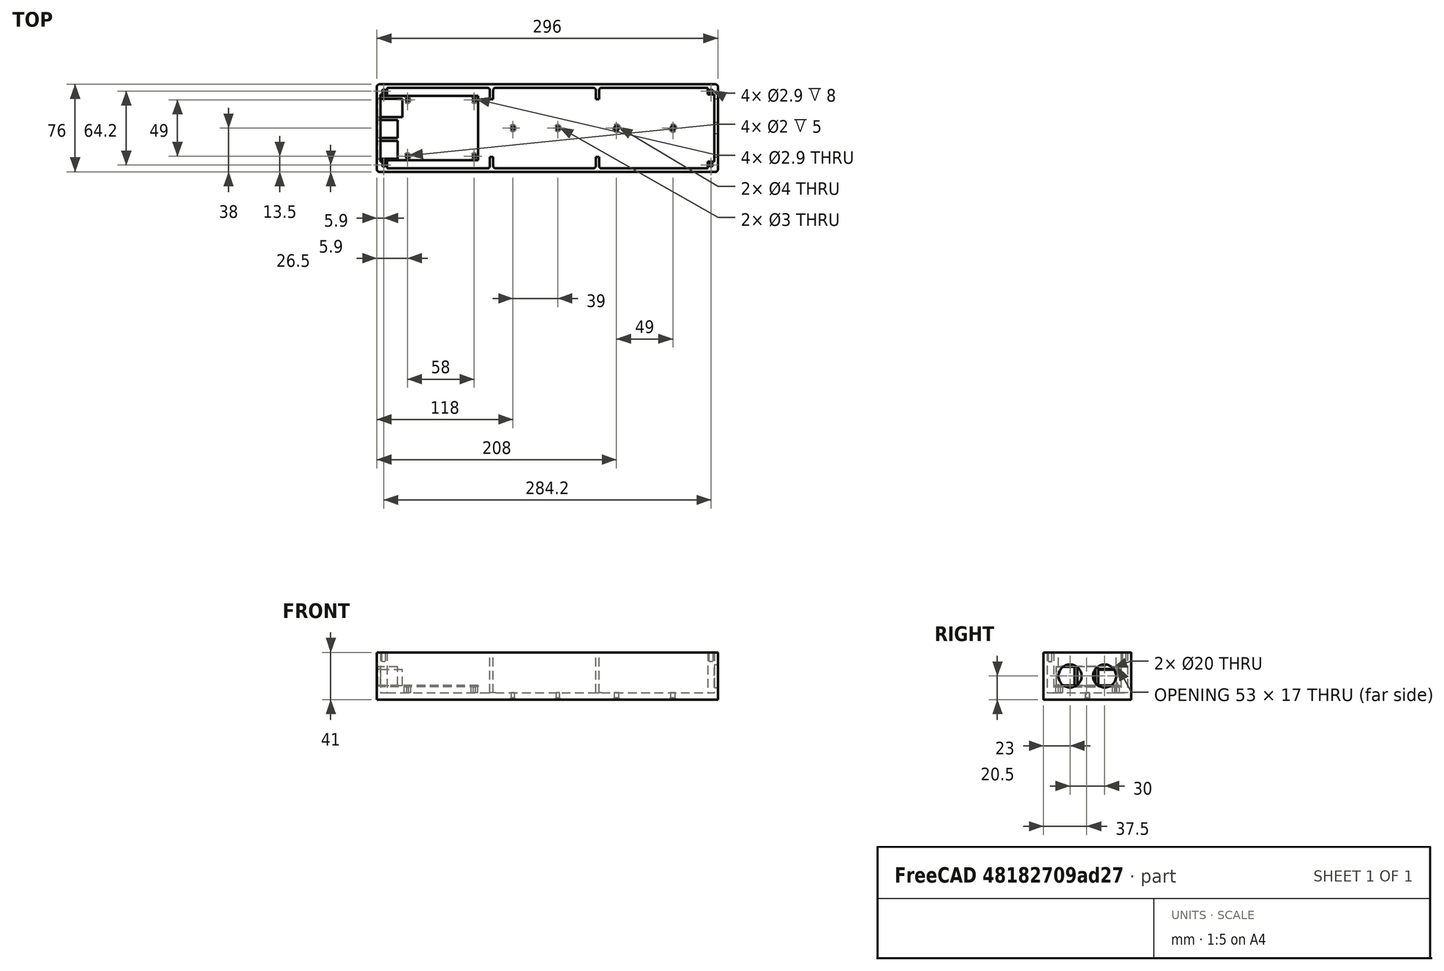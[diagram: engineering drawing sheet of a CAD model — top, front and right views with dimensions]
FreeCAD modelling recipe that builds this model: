
FCSTD DOCUMENT  (FreeCAD 0.19R24276 (Git))
Label: Octopi Enclosure
License: All rights reserved
LicenseURL: http://en.wikipedia.org/wiki/All_rights_reserved
objects: Sketcher::SketchObject×12, PartDesign::Pad×6, PartDesign::Pocket×5, PartDesign::Body×2, PartDesign::Fillet×2, TechDraw::DrawViewDimension×2, Spreadsheet::Sheet×1, PartDesign::Chamfer×1, TechDraw::DrawSVGTemplate×1, TechDraw::DrawViewPart×1, TechDraw::DrawPage×1
note: 42 computed .brp shape members not serialized (recipe doc carries the construction recipe); baked Part::Feature solids carry a one-line shape summary decoded from their .brp

FEATURE [Spreadsheet::Sheet] Spreadsheet
  cells = A2=Internal length; B2(Length)=290; C2=Length; A3=Internal width; B3(Width)=70; C3=Width; A4=Internal height; B4(Height)=35; C4=Height; A5=Wall thickness; B5(Wall)=3; C5=Wall; A6=Lid screw dia; B6(LidScrewDia)=2.9; C6=LidScrewDia; A7=Corner radius; B7(CornerRadius)=2; C7=CornerRadius
FEATURE [Sketcher::SketchObject] Sketch  label="External"
  FullyConstrained = true
  MapMode = 5
  Support = -> [XY_Plane]
  expr: Constraints[8] = <<Spreadsheet>>.Wall
  expr: Constraints[9] = <<Spreadsheet>>.Wall
  expr: Constraints[10] = <<Spreadsheet>>.Width + <<Spreadsheet>>.Wall * 2
  expr: Constraints[11] = <<Spreadsheet>>.Length + <<Spreadsheet>>.Wall * 2
  sketch-geometry (4):
    g0: LineSegment StartX=-3 StartY=73 StartZ=0 EndX=293 EndY=73 EndZ=0
    g1: LineSegment StartX=293 StartY=73 StartZ=0 EndX=293 EndY=-3 EndZ=0
    g2: LineSegment StartX=293 StartY=-3 StartZ=0 EndX=-3 EndY=-3 EndZ=0
    g3: LineSegment StartX=-3 StartY=-3 StartZ=0 EndX=-3 EndY=73 EndZ=0
  constraints (12):
    c: Coincident(g0,g1)
    c: Coincident(g1,g2)
    c: Coincident(g2,g3)
    c: Coincident(g3,g0)
    c: Horizontal(g0)
    c: Horizontal(g2)
    c: Vertical(g1)
    c: Vertical(g3)
    c: DistanceY(g2,g-1) = 3
    c: DistanceX(g2,g-1) = 3
    c: DistanceY(g3,g3) = 76
    c: DistanceX(g0,g0) = 296
FEATURE [PartDesign::Pad] Pad  label="Body001"
  Direction = (1,1,1)
  Length = 41
  Length2 = 100
  Profile = -> Sketch
  Type = 0
  expr: Length = <<Spreadsheet>>.Height + <<Spreadsheet>>.Wall * 2
FEATURE [Sketcher::SketchObject] Sketch001  label="Internal"
  FullyConstrained = true
  MapMode = 5
  Placement = pos=(0,0,41) rot=(0,0,1;0rad)
  Support = -> [Pad]
  expr: Constraints[26] = <<Spreadsheet>>.Width
  expr: Constraints[27] = <<Spreadsheet>>.Length
  expr: Constraints[28] = <<Spreadsheet>>.LidScrewDia * 2
  sketch-geometry (12):
    g0: LineSegment StartX=5.8 StartY=70 StartZ=0 EndX=284.2 EndY=70 EndZ=0
    g1: LineSegment StartX=284.2 StartY=70 StartZ=0 EndX=284.2 EndY=64.2 EndZ=0
    g2: LineSegment StartX=284.2 StartY=64.2 StartZ=0 EndX=290 EndY=64.2 EndZ=0
    g3: LineSegment StartX=290 StartY=64.2 StartZ=0 EndX=290 EndY=5.8 EndZ=0
    g4: LineSegment StartX=290 StartY=5.8 StartZ=0 EndX=284.2 EndY=5.8 EndZ=0
    g5: LineSegment StartX=284.2 StartY=5.8 StartZ=0 EndX=284.2 EndY=0 EndZ=0
    g6: LineSegment StartX=284.2 StartY=0 StartZ=0 EndX=5.8 EndY=0 EndZ=0
    g7: LineSegment StartX=5.8 StartY=0 StartZ=0 EndX=5.8 EndY=5.8 EndZ=0
    g8: LineSegment StartX=5.8 StartY=5.8 StartZ=0 EndX=0 EndY=5.8 EndZ=0
    g9: LineSegment StartX=0 StartY=5.8 StartZ=0 EndX=0 EndY=64.2 EndZ=0
    g10: LineSegment StartX=0 StartY=64.2 StartZ=0 EndX=5.8 EndY=64.2 EndZ=0
    g11: LineSegment StartX=5.8 StartY=70 StartZ=0 EndX=5.8 EndY=64.2 EndZ=0
  constraints (36):
    c: Horizontal(g0)
    c: Coincident(g0,g1)
    c: Vertical(g1)
    c: Coincident(g1,g2)
    c: Horizontal(g2)
    c: Coincident(g2,g3)
    c: Vertical(g3)
    c: Coincident(g3,g4)
    c: Horizontal(g4)
    c: Coincident(g4,g5)
    c: Vertical(g5)
    c: Coincident(g5,g6)
    c: Horizontal(g6)
    c: Coincident(g6,g7)
    c: Vertical(g7)
    c: Coincident(g7,g8)
    c: Horizontal(g8)
    c: Coincident(g8,g9)
    c: Vertical(g9)
    c: Coincident(g9,g10)
    c: Horizontal(g10)
    c: Coincident(g11,g0)
    c: Coincident(g11,g10)
    c: Vertical(g11)
    c: PointOnObject(g8,g-2)
    c: PointOnObject(g6,g-1)
    c: DistanceY(g6,g0) = 70
    c: DistanceX(g8,g3) = 290
    c: DistanceY(g7,g7) = 5.8
    c: Equal(g7,g8)
    c: Equal(g10,g7)
    c: Equal(g11,g7)
    c: Equal(g7,g5)
    c: Equal(g5,g4)
    c: Equal(g5,g2)
    c: Equal(g5,g1)
FEATURE [PartDesign::Pocket] Pocket  label="Inside space"
  BaseFeature = -> Pad
  Length = 35
  Length2 = 100
  Profile = -> Sketch001
  Type = 0
  expr: Length = <<Spreadsheet>>.Height
FEATURE [Sketcher::SketchObject] Sketch002  label="Raspberry PI"
  AttachmentOffset = pos=(85,63,0) rot=(0,0,1;3.14159rad)
  FullyConstrained = true
  MapMode = 5
  Placement = pos=(85,63,6) rot=(0,0,1;3.14159rad)
  Support = -> [Pocket]
  expr: Constraints[10] = <<Spreadsheet>>.LidScrewDia
  expr: Constraints[18] = 6
  expr: .AttachmentOffset.Base.y = 56 + (<<Spreadsheet>>.Width - 56) / 2
  sketch-geometry (12):
    g0: LineSegment StartX=0 StartY=0 StartZ=0 EndX=85 EndY=0 EndZ=0
    g1: LineSegment StartX=85 StartY=0 StartZ=0 EndX=85 EndY=56 EndZ=0
    g2: LineSegment StartX=85 StartY=56 StartZ=0 EndX=0 EndY=56 EndZ=0
    g3: LineSegment StartX=0 StartY=56 StartZ=0 EndX=0 EndY=0 EndZ=0
    g4: Circle CenterX=3.5 CenterY=3.5 CenterZ=0 NormalX=0 NormalY=0 NormalZ=1 AngleXU=0 Radius=1.45
    g5: Circle CenterX=3.5 CenterY=52.5 CenterZ=0 NormalX=0 NormalY=0 NormalZ=1 AngleXU=0 Radius=1.45
    g6: Circle CenterX=61.5 CenterY=52.5 CenterZ=0 NormalX=0 NormalY=0 NormalZ=1 AngleXU=0 Radius=1.45
    g7: Circle CenterX=61.5 CenterY=3.5 CenterZ=0 NormalX=0 NormalY=0 NormalZ=1 AngleXU=0 Radius=1.45
    g8: Circle CenterX=3.5 CenterY=3.5 CenterZ=0 NormalX=0 NormalY=0 NormalZ=1 AngleXU=0 Radius=3
    g9: Circle CenterX=3.5 CenterY=52.5 CenterZ=0 NormalX=0 NormalY=0 NormalZ=1 AngleXU=0 Radius=3
    g10: Circle CenterX=61.5 CenterY=3.5 CenterZ=0 NormalX=0 NormalY=0 NormalZ=1 AngleXU=0 Radius=3
    g11: Circle CenterX=61.5 CenterY=52.5 CenterZ=0 NormalX=0 NormalY=0 NormalZ=1 AngleXU=0 Radius=3
  constraints (31):
    c: Coincident(g0,g1)
    c: Coincident(g1,g2)
    c: Coincident(g2,g3)
    c: Coincident(g3,g0)
    c: Horizontal(g0)
    c: Horizontal(g2)
    c: Vertical(g1)
    c: Vertical(g3)
    c: DistanceX(g2,g2) = 85
    c: DistanceY(g1,g1) = 56
    c: Diameter(g4) = 2.9
    c: DistanceX(g0,g4) = 3.5
    c: DistanceY(g0,g4) = 3.5
    c: Equal(g4,g5)
    c: Equal(g5,g6)
    c: Equal(g6,g7)
    c: DistanceY(g5,g2) = 3.5
    c: Coincident(g8,g4)
    c: Diameter(g8) = 6
    c: Equal(g9,g11)
    c: Equal(g11,g10)
    c: Equal(g10,g8)
    c: Coincident(g9,g5)
    c: Coincident(g11,g6)
    c: Coincident(g10,g7)
    c: Coincident(g0,g-1)
    c: DistanceX(g4,g7) = 58
    c: Vertical(g7,g6)
    c: Horizontal(g5,g6)
    c: Horizontal(g4,g7)
    c: Vertical(g5,g4)
FEATURE [Sketcher::SketchObject] Sketch003  label="Raspberry PI001"
  AttachmentOffset = pos=(85,63,0) rot=(0,0,1;3.14159rad)
  FullyConstrained = true
  expr: .AttachmentOffset.Base.y = 56 + (<<Spreadsheet>>.Width - 56) / 2
  expr: Constraints[10] = <<Spreadsheet>>.LidScrewDia
  sketch-geometry (8):
    g0: LineSegment StartX=0 StartY=0 StartZ=0 EndX=85 EndY=0 EndZ=0
    g1: LineSegment StartX=85 StartY=0 StartZ=0 EndX=85 EndY=56 EndZ=0
    g2: LineSegment StartX=85 StartY=56 StartZ=0 EndX=0 EndY=56 EndZ=0
    g3: LineSegment StartX=0 StartY=56 StartZ=0 EndX=0 EndY=0 EndZ=0
    g4: Circle CenterX=3.5 CenterY=3.5 CenterZ=0 NormalX=0 NormalY=0 NormalZ=1 AngleXU=0 Radius=1.45
    g5: Circle CenterX=3.5 CenterY=52.5 CenterZ=0 NormalX=0 NormalY=0 NormalZ=1 AngleXU=0 Radius=1.45
    g6: Circle CenterX=61.5 CenterY=52.5 CenterZ=0 NormalX=0 NormalY=0 NormalZ=1 AngleXU=0 Radius=1.45
    g7: Circle CenterX=61.5 CenterY=3.5 CenterZ=0 NormalX=0 NormalY=0 NormalZ=1 AngleXU=0 Radius=1.45
  constraints (23):
    c: Coincident(g0,g1)
    c: Coincident(g1,g2)
    c: Coincident(g2,g3)
    c: Coincident(g3,g0)
    c: Horizontal(g0)
    c: Horizontal(g2)
    c: Vertical(g1)
    c: Vertical(g3)
    c: DistanceX(g2,g2) = 85
    c: DistanceY(g1,g1) = 56
    c: Diameter(g4) = 2.9
    c: DistanceX(g0,g4) = 3.5
    c: DistanceY(g0,g4) = 3.5
    c: Equal(g4,g5)
    c: Equal(g5,g6)
    c: Equal(g6,g7)
    c: DistanceY(g5,g2) = 3.5
    c: Coincident(g0,g-1)
    c: DistanceX(g4,g7) = 58
    c: Vertical(g7,g6)
    c: Horizontal(g5,g6)
    c: Horizontal(g4,g7)
    c: Vertical(g5,g4)
FEATURE [PartDesign::Pad] Pad001  label="PCB"
  Direction = (1,1,1)
  Length = 1.5
  Length2 = 100
  Profile = -> Sketch003
  Reversed = true
  Type = 0
FEATURE [Sketcher::SketchObject] Sketch004  label="Ethernet"
  FullyConstrained = true
  MapMode = 5
  Support = -> [XY_Plane002]
  expr: Constraints[11] = 87
  sketch-geometry (4):
    g0: LineSegment StartX=65.8 StartY=18.5 StartZ=0 EndX=87 EndY=18.5 EndZ=0
    g1: LineSegment StartX=87 StartY=18.5 StartZ=0 EndX=87 EndY=2.5 EndZ=0
    g2: LineSegment StartX=87 StartY=2.5 StartZ=0 EndX=65.8 EndY=2.5 EndZ=0
    g3: LineSegment StartX=65.8 StartY=2.5 StartZ=0 EndX=65.8 EndY=18.5 EndZ=0
  constraints (12):
    c: Coincident(g0,g1)
    c: Coincident(g1,g2)
    c: Coincident(g2,g3)
    c: Coincident(g3,g0)
    c: Horizontal(g0)
    c: Horizontal(g2)
    c: Vertical(g1)
    c: Vertical(g3)
    c: DistanceY(g1,g1) = 16
    c: DistanceX(g0,g0) = 21.2
    c: DistanceY(g-1,g1) = 2.5
    c: DistanceX(g-1,g1) = 87
FEATURE [PartDesign::Pad] Pad002  label="Ethernet001"
  BaseFeature = -> Pad001
  Direction = (1,1,1)
  Length = 13.5
  Length2 = 100
  Profile = -> Sketch004
  Type = 0
FEATURE [Sketcher::SketchObject] Sketch005  label="Connector holes"
  FullyConstrained = true
  MapMode = 5
  Placement = pos=(-3,0,0) rot=(0.57735,-0.57735,-0.57735;2.0944rad)
  Support = -> [Pocket]
  sketch-geometry (18):
    g0: LineSegment StartX=-61 StartY=26.5 StartZ=0 EndX=-44 EndY=26.5 EndZ=0
    g1: LineSegment StartX=-44 StartY=26.5 StartZ=0 EndX=-44 EndY=12 EndZ=0
    g2: LineSegment StartX=-44 StartY=12 StartZ=0 EndX=-61 EndY=12 EndZ=0
    g3: LineSegment StartX=-61 StartY=12 StartZ=0 EndX=-61 EndY=26.5 EndZ=0
    g4: LineSegment StartX=-42.5 StartY=29 StartZ=0 EndX=-26 EndY=29 EndZ=0
    g5: LineSegment StartX=-26 StartY=29 StartZ=0 EndX=-26 EndY=12 EndZ=0
    g6: LineSegment StartX=-26 StartY=12 StartZ=0 EndX=-42.5 EndY=12 EndZ=0
    g7: LineSegment StartX=-42.5 StartY=12 StartZ=0 EndX=-42.5 EndY=29 EndZ=0
    g8: LineSegment StartX=-24.5 StartY=29 StartZ=0 EndX=-8 EndY=29 EndZ=0
    g9: LineSegment StartX=-8 StartY=29 StartZ=0 EndX=-8 EndY=12 EndZ=0
    g10: LineSegment StartX=-8 StartY=12 StartZ=0 EndX=-24.5 EndY=12 EndZ=0
    g11: LineSegment StartX=-24.5 StartY=12 StartZ=0 EndX=-24.5 EndY=29 EndZ=0
    g12: LineSegment StartX=-61 StartY=26.5 StartZ=0 EndX=-44 EndY=26.5 EndZ=0
    g13: LineSegment StartX=-44 StartY=26.5 StartZ=0 EndX=-42.5 EndY=29 EndZ=0
    g14: LineSegment StartX=-42.5 StartY=29 StartZ=0 EndX=-8 EndY=29 EndZ=0
    g15: LineSegment StartX=-8 StartY=29 StartZ=0 EndX=-8 EndY=12 EndZ=0
    g16: LineSegment StartX=-8 StartY=12 StartZ=0 EndX=-61 EndY=12 EndZ=0
    g17: LineSegment StartX=-61 StartY=12 StartZ=0 EndX=-61 EndY=26.5 EndZ=0
  constraints (48):
    c: Coincident(g0,g1)
    c: Coincident(g1,g2)
    c: Coincident(g2,g3)
    c: Coincident(g3,g0)
    c: Horizontal(g0)
    c: Horizontal(g2)
    c: Vertical(g1)
    c: Vertical(g3)
    c: DistanceX(g0,g0) = 17
    c: DistanceY(g1,g1) = 14.5
    c: DistanceY(g-1,g1) = 12
    c: DistanceX(g1,g-1) = 44
    c: Coincident(g4,g5)
    c: Coincident(g5,g6)
    c: Coincident(g6,g7)
    c: Coincident(g7,g4)
    c: Horizontal(g4)
    c: Horizontal(g6)
    c: Vertical(g5)
    c: Vertical(g7)
    c: DistanceY(g5,g5) = 17
    c: DistanceX(g4,g4) = 16.5
    c: DistanceX(g1,g6) = 1.5
    c: Horizontal(g1,g6)
    c: Coincident(g8,g9)
    c: Coincident(g9,g10)
    c: Coincident(g10,g11)
    c: Coincident(g11,g8)
    c: Horizontal(g8)
    c: Horizontal(g10)
    c: Vertical(g9)
    c: Vertical(g11)
    c: Equal(g4,g8)
    c: Equal(g5,g11)
    c: Horizontal(g10,g5)
    c: DistanceX(g4,g8) = 1.5
    c: Coincident(g0,g12)
    c: Coincident(g12,g0)
    c: Coincident(g12,g13)
    c: Coincident(g13,g4)
    c: Coincident(g13,g14)
    c: Coincident(g14,g8)
    c: Coincident(g14,g15)
    c: Coincident(g15,g9)
    c: Coincident(g15,g16)
    c: Coincident(g16,g2)
    c: Coincident(g16,g17)
    c: Coincident(g17,g12)
FEATURE [PartDesign::Pocket] Pocket001  label="Connector holes x3"
  BaseFeature = -> Pocket
  Length = 5
  Length2 = 100
  Profile = -> Sketch005
  Type = 2
FEATURE [Sketcher::SketchObject] Sketch007  label="USB"
  FullyConstrained = true
  MapMode = 5
  Support = -> [XY_Plane002]
  expr: Constraints[11] = 87
  sketch-geometry (8):
    g0: LineSegment StartX=70 StartY=36.5 StartZ=0 EndX=87 EndY=36.5 EndZ=0
    g1: LineSegment StartX=87 StartY=36.5 StartZ=0 EndX=87 EndY=21 EndZ=0
    g2: LineSegment StartX=87 StartY=21 StartZ=0 EndX=70 EndY=21 EndZ=0
    g3: LineSegment StartX=70 StartY=21 StartZ=0 EndX=70 EndY=36.5 EndZ=0
    g4: LineSegment StartX=70 StartY=54.5 StartZ=0 EndX=87 EndY=54.5 EndZ=0
    g5: LineSegment StartX=87 StartY=54.5 StartZ=0 EndX=87 EndY=39 EndZ=0
    g6: LineSegment StartX=87 StartY=39 StartZ=0 EndX=70 EndY=39 EndZ=0
    g7: LineSegment StartX=70 StartY=39 StartZ=0 EndX=70 EndY=54.5 EndZ=0
  constraints (24):
    c: Coincident(g0,g1)
    c: Coincident(g1,g2)
    c: Coincident(g2,g3)
    c: Coincident(g3,g0)
    c: Horizontal(g0)
    c: Horizontal(g2)
    c: Vertical(g1)
    c: Vertical(g3)
    c: DistanceY(g1,g1) = 15.5
    c: DistanceX(g0,g0) = 17
    c: DistanceY(g-1,g1) = 21
    c: DistanceX(g-1,g1) = 87
    c: Coincident(g4,g5)
    c: Coincident(g5,g6)
    c: Coincident(g6,g7)
    c: Coincident(g7,g4)
    c: Horizontal(g4)
    c: Horizontal(g6)
    c: Vertical(g5)
    c: Vertical(g7)
    c: Equal(g4,g0)
    c: Equal(g5,g1)
    c: Vertical(g5,g1)
    c: DistanceY(g-1,g5) = 39
FEATURE [PartDesign::Pad] Pad003  label="USB x2"
  BaseFeature = -> Pad002
  Direction = (1,1,1)
  Length = 16
  Length2 = 100
  Profile = -> Sketch007
  Type = 0
FEATURE [PartDesign::Body] Body002  label="Raspberry PI002"
  Group = -> [Sketch003,Pad001,Sketch004,Pad002,Sketch007,Pad003]
  Origin = -> Origin002
  Placement = pos=(85,63,12.5) rot=(0,0,1;3.14159rad)
  Tip = -> Pad003
  expr: .Placement.Base.y = 56 + (<<Spreadsheet>>.Width - 56) / 2
  expr: .Placement.Base.z = 7.5 + 5
FEATURE [Sketcher::SketchObject] Sketch008  label="PI fixing pillers"
  FullyConstrained = true
  MapMode = 5
  Placement = pos=(0,0,6) rot=(0,0,1;0rad)
  Support = -> [Pocket001]
  sketch-geometry (8):
    g0: Circle CenterX=23.5 CenterY=10.5 CenterZ=0 NormalX=0 NormalY=0 NormalZ=1 AngleXU=0 Radius=1
    g1: Circle CenterX=23.5 CenterY=10.5 CenterZ=0 NormalX=0 NormalY=0 NormalZ=1 AngleXU=0 Radius=3
    g2: Circle CenterX=23.5 CenterY=59.5 CenterZ=0 NormalX=0 NormalY=0 NormalZ=1 AngleXU=0 Radius=1
    g3: Circle CenterX=23.5 CenterY=59.5 CenterZ=0 NormalX=0 NormalY=0 NormalZ=1 AngleXU=0 Radius=3
    g4: Circle CenterX=81.5 CenterY=59.5 CenterZ=0 NormalX=0 NormalY=0 NormalZ=1 AngleXU=0 Radius=1
    g5: Circle CenterX=81.5 CenterY=59.5 CenterZ=0 NormalX=0 NormalY=0 NormalZ=1 AngleXU=0 Radius=3
    g6: Circle CenterX=81.5 CenterY=10.5 CenterZ=0 NormalX=0 NormalY=0 NormalZ=1 AngleXU=0 Radius=1
    g7: Circle CenterX=81.5 CenterY=10.5 CenterZ=0 NormalX=0 NormalY=0 NormalZ=1 AngleXU=0 Radius=3
  constraints (20):
    c: Diameter(g0) = 2
    c: DistanceX(g-1,g0) = 23.5
    c: DistanceY(g-1,g0) = 10.5
    c: Diameter(g1) = 6
    c: Coincident(g1,g0)
    c: Vertical(g2,g0)
    c: Vertical(g7,g5)
    c: Horizontal(g0,g6)
    c: Coincident(g6,g7)
    c: Coincident(g4,g5)
    c: Coincident(g2,g3)
    c: Equal(g1,g3)
    c: Equal(g3,g5)
    c: Equal(g5,g7)
    c: Equal(g0,g2)
    c: Equal(g2,g4)
    c: Equal(g4,g6)
    c: DistanceY(g0,g4) = 49
    c: DistanceX(g2,g4) = 58
    c: Horizontal(g2,g4)
FEATURE [PartDesign::Pad] Pad004  label="PI Fixings"
  BaseFeature = -> Pocket001
  Direction = (1,1,1)
  Length = 5
  Length2 = 100
  Profile = -> Sketch008
  Type = 0
FEATURE [Sketcher::SketchObject] Sketch009
  FullyConstrained = false
  MapMode = 5
  Support = -> [XY_Plane]
  expr: Constraints[5] = <<Spreadsheet>>.Width / 2
  sketch-geometry (5):
    g0: Circle CenterX=115 CenterY=35 CenterZ=0 NormalX=0 NormalY=0 NormalZ=1 AngleXU=0 Radius=1.5
    g1: Circle CenterX=154 CenterY=35 CenterZ=0 NormalX=0 NormalY=0 NormalZ=1 AngleXU=0 Radius=1.5
    g2: LineSegment StartX=0 StartY=35 StartZ=0 EndX=314.836 EndY=35 EndZ=0
    g3: Circle CenterX=205 CenterY=35 CenterZ=0 NormalX=0 NormalY=0 NormalZ=1 AngleXU=0 Radius=2
    g4: Circle CenterX=254 CenterY=35 CenterZ=0 NormalX=0 NormalY=0 NormalZ=1 AngleXU=0 Radius=2
  constraints (15):
    c: Diameter(g0) = 3
    c: Equal(g0,g1)
    c: Horizontal(g0,g1)
    c: DistanceX(g0,g1) = 39
    c: Horizontal(g2)
    c: DistanceY(g-1,g2) = 35
    c: Vertical(g2,g-1)
    c: PointOnObject(g0,g2)
    c: DistanceX(g-1,g0) = 115
    c: Horizontal(g3,g4)
    c: Diameter(g3) = 4
    c: Equal(g3,g4)
    c: PointOnObject(g3,g2)
    c: DistanceX(g3,g4) = 49
    c: DistanceX(g-1,g3) = 205
FEATURE [PartDesign::Pocket] Pocket002  label="PSU and Relay mounting holes"
  BaseFeature = -> Pad004
  Length = 5
  Length2 = 100
  Profile = -> Sketch009
  Reversed = true
  Type = 1
FEATURE [Sketcher::SketchObject] Sketch010
  FullyConstrained = true
  MapMode = 5
  Placement = pos=(0,0,41) rot=(0,0,1;0rad)
  Support = -> [Pocket002]
  expr: Constraints[0] = <<Spreadsheet>>.LidScrewDia
  expr: Constraints[1] = <<Spreadsheet>>.LidScrewDia
  expr: Constraints[2] = <<Spreadsheet>>.LidScrewDia
  expr: Constraints[10] = <<Spreadsheet>>.Length - <<Spreadsheet>>.LidScrewDia
  expr: Constraints[11] = <<Spreadsheet>>.Width - <<Spreadsheet>>.LidScrewDia * 2
  sketch-geometry (4):
    g0: Circle CenterX=2.9 CenterY=2.9 CenterZ=0 NormalX=0 NormalY=0 NormalZ=1 AngleXU=0 Radius=1.45
    g1: Circle CenterX=2.9 CenterY=67.1 CenterZ=0 NormalX=0 NormalY=0 NormalZ=1 AngleXU=0 Radius=1.45
    g2: Circle CenterX=287.1 CenterY=2.9 CenterZ=0 NormalX=0 NormalY=0 NormalZ=1 AngleXU=0 Radius=1.45
    g3: Circle CenterX=287.1 CenterY=67.1 CenterZ=0 NormalX=0 NormalY=0 NormalZ=1 AngleXU=0 Radius=1.45
  constraints (12):
    c: Diameter(g0) = 2.9
    c: DistanceX(g-1,g0) = 2.9
    c: DistanceY(g-1,g0) = 2.9
    c: Equal(g0,g1) = 2.9
    c: Equal(g0,g2) = 2.9
    c: Equal(g0,g3)
    c: Vertical(g1,g0)
    c: Horizontal(g0,g2)
    c: Vertical(g3,g2)
    c: Horizontal(g1,g3)
    c: DistanceX(g-1,g2) = 287.1
    c: DistanceY(g0,g1) = 64.2
FEATURE [PartDesign::Pocket] Pocket003
  BaseFeature = -> Pocket002
  Length = 8
  Length2 = 100
  Profile = -> Sketch010
  Type = 0
FEATURE [PartDesign::Fillet] Fillet
  Base = -> Pocket003 [Edge5,Edge16,Edge1,Edge2]
  BaseFeature = -> Pocket003
  Radius = 2
  SupportTransform = false
  expr: Radius = <<Spreadsheet>>.CornerRadius
FEATURE [Sketcher::SketchObject] Sketch011
  FullyConstrained = true
  MapMode = 5
  Placement = pos=(293,0,0) rot=(0.57735,0.57735,0.57735;2.0944rad)
  Support = -> [Fillet]
  expr: Constraints[1] = <<Spreadsheet>>.Height / 2 + <<Spreadsheet>>.Wall
  expr: Constraints[5] = <<Spreadsheet>>.Width - 20
  sketch-geometry (2):
    g0: Circle CenterX=20 CenterY=20.5 CenterZ=0 NormalX=0 NormalY=0 NormalZ=1 AngleXU=0 Radius=10
    g1: Circle CenterX=50 CenterY=20.5 CenterZ=0 NormalX=0 NormalY=0 NormalZ=1 AngleXU=0 Radius=10
  constraints (6):
    c: Diameter(g0) = 20
    c: DistanceY(g-1,g0) = 20.5
    c: DistanceX(g-1,g0) = 20
    c: Equal(g0,g1)
    c: Horizontal(g0,g1)
    c: DistanceX(g-1,g1) = 50
FEATURE [PartDesign::Pocket] Pocket004
  BaseFeature = -> Fillet
  Length = 5
  Length2 = 100
  Profile = -> Sketch011
  Type = 2
FEATURE [PartDesign::Chamfer] Chamfer
  Angle = 45
  Base = -> Pocket004 [Edge15,Edge14,Edge13,Edge12]
  BaseFeature = -> Pocket004
  ChamferType = 0
  FlipDirection = false
  Size = 1.5
  Size2 = 1
  SupportTransform = false
FEATURE [Sketcher::SketchObject] Sketch012
  FullyConstrained = true
  MapMode = 5
  Placement = pos=(0,0,6) rot=(0,0,1;0rad)
  Support = -> [Chamfer]
  expr: Constraints[10] = 10
  expr: Constraints[43] = <<Spreadsheet>>.Width
  sketch-geometry (16):
    g0: LineSegment StartX=95 StartY=10 StartZ=0 EndX=98 EndY=10 EndZ=0
    g1: LineSegment StartX=98 StartY=10 StartZ=0 EndX=98 EndY=0 EndZ=0
    g2: LineSegment StartX=98 StartY=0 StartZ=0 EndX=95 EndY=0 EndZ=0
    g3: LineSegment StartX=95 StartY=0 StartZ=0 EndX=95 EndY=10 EndZ=0
    g4: LineSegment StartX=190 StartY=10 StartZ=0 EndX=187 EndY=10 EndZ=0
    g5: LineSegment StartX=187 StartY=10 StartZ=0 EndX=187 EndY=0 EndZ=0
    g6: LineSegment StartX=187 StartY=0 StartZ=0 EndX=190 EndY=0 EndZ=0
    g7: LineSegment StartX=190 StartY=0 StartZ=0 EndX=190 EndY=10 EndZ=0
    g8: LineSegment StartX=95 StartY=70 StartZ=0 EndX=98 EndY=70 EndZ=0
    g9: LineSegment StartX=98 StartY=70 StartZ=0 EndX=98 EndY=60 EndZ=0
    g10: LineSegment StartX=98 StartY=60 StartZ=0 EndX=95 EndY=60 EndZ=0
    g11: LineSegment StartX=95 StartY=60 StartZ=0 EndX=95 EndY=70 EndZ=0
    g12: LineSegment StartX=190 StartY=70 StartZ=0 EndX=187 EndY=70 EndZ=0
    g13: LineSegment StartX=187 StartY=70 StartZ=0 EndX=187 EndY=60 EndZ=0
    g14: LineSegment StartX=187 StartY=60 StartZ=0 EndX=190 EndY=60 EndZ=0
    g15: LineSegment StartX=190 StartY=60 StartZ=0 EndX=190 EndY=70 EndZ=0
  constraints (48):
    c: Coincident(g0,g1)
    c: Coincident(g1,g2)
    c: Coincident(g2,g3)
    c: Coincident(g3,g0)
    c: Horizontal(g0)
    c: Horizontal(g2)
    c: Vertical(g1)
    c: Vertical(g3)
    c: DistanceX(g0,g0) = 3
    c: Horizontal(g2,g-1)
    c: DistanceY(g1,g1) = 10
    c: DistanceX(g-1,g2) = 95
    c: Coincident(g4,g5)
    c: Coincident(g5,g6)
    c: Coincident(g6,g7)
    c: Coincident(g7,g4)
    c: Horizontal(g4)
    c: Horizontal(g6)
    c: Vertical(g5)
    c: Vertical(g7)
    c: Equal(g0,g4)
    c: Equal(g1,g5)
    c: Horizontal(g6,g2)
    c: DistanceX(g-1,g6) = 190
    c: Coincident(g8,g9)
    c: Coincident(g9,g10)
    c: Coincident(g10,g11)
    c: Coincident(g11,g8)
    c: Horizontal(g8)
    c: Horizontal(g10)
    c: Vertical(g9)
    c: Vertical(g11)
    c: Equal(g0,g8) = 3
    c: Equal(g1,g9) = 10
    c: Coincident(g12,g13)
    c: Coincident(g13,g14)
    c: Coincident(g14,g15)
    c: Coincident(g15,g12)
    c: Horizontal(g12)
    c: Horizontal(g14)
    c: Vertical(g13)
    c: Vertical(g15)
    c: Horizontal(g9,g13)
    c: DistanceY(g-1,g8) = 70
    c: Equal(g11,g13)
    c: Vertical(g10,g2)
    c: Vertical(g13,g5)
    c: Equal(g2,g14)
FEATURE [PartDesign::Pad] Pad005
  BaseFeature = -> Chamfer
  Direction = (1,1,1)
  Length = 35
  Length2 = 100
  Profile = -> Sketch012
  Type = 0
  expr: Length = <<Spreadsheet>>.Height
FEATURE [TechDraw::DrawSVGTemplate] Template
  EditableTexts = Designed_by_Name=Designed by Name; Drawing_number=Drawing number; FC-Date=Date; FC-SC=Scale; FC-SH=Sheet; FC-Title=Octopi enclosure; Subtitle=Subtitle; Weight=Weight
  Height = 210
  Orientation = 1
  Width = 297
FEATURE [PartDesign::Fillet] Fillet001
  Base = -> Pad005 [Edge162,Edge158,Edge131,Edge136,Edge137,Edge142,Edge157,Edge153]
  BaseFeature = -> Pad005
  Radius = 2
  SupportTransform = false
FEATURE [PartDesign::Body] Body
  Group = -> [Sketch,Pad,Sketch001,Pocket,Sketch002,Sketch005,Pocket001,Sketch008,Pad004,Sketch009,Pocket002,Sketch010,Pocket003,Fillet,Sketch011,Pocket004,Chamfer,Sketch012,Pad005,Fillet001]
  Origin = -> Origin
  Tip = -> Fillet001
FEATURE [TechDraw::DrawViewPart] View
  CoarseView = false
  Direction = (0,0,1)
  Focus = 100
  HardHidden = false
  IsoCount = 0
  IsoHidden = false
  IsoVisible = false
  LockPosition = false
  Perspective = false
  Rotation = 0
  ScaleType = 0
  SeamHidden = false
  SeamVisible = true
  SmoothHidden = false
  SmoothVisible = true
  Source = -> [Body]
  X = 148.5
  XDirection = (1,0,0)
  Y = 105
FEATURE [TechDraw::DrawViewDimension] Dimension
  Arbitrary = false
  ArbitraryTolerances = false
  EqualTolerance = true
  FormatSpec = %.2f
  FormatSpecOverTolerance = %+.2f
  FormatSpecUnderTolerance = %+.2f
  Inverted = false
  LockPosition = false
  MeasureType = 1
  OverTolerance = 0
  References2D = -> [View]
  Rotation = 0
  ScaleType = 0
  TheoreticalExact = false
  Type = 1
  UnderTolerance = 0
  X = -1.41808
  Y = 61.8158
FEATURE [TechDraw::DrawViewDimension] Dimension001
  Arbitrary = false
  ArbitraryTolerances = false
  EqualTolerance = true
  FormatSpec = %.2f
  FormatSpecOverTolerance = %+.2f
  FormatSpecUnderTolerance = %+.2f
  Inverted = false
  LockPosition = false
  MeasureType = 1
  OverTolerance = 0
  References2D = -> [View]
  Rotation = 0
  ScaleType = 0
  TheoreticalExact = false
  Type = 2
  UnderTolerance = 0
  X = -139.2
  Y = 0
FEATURE [TechDraw::DrawPage] Page
  KeepUpdated = true
  NextBalloonIndex = 1
  ProjectionType = 0
  Template = -> Template
  Views = -> [View,Dimension,Dimension001]
